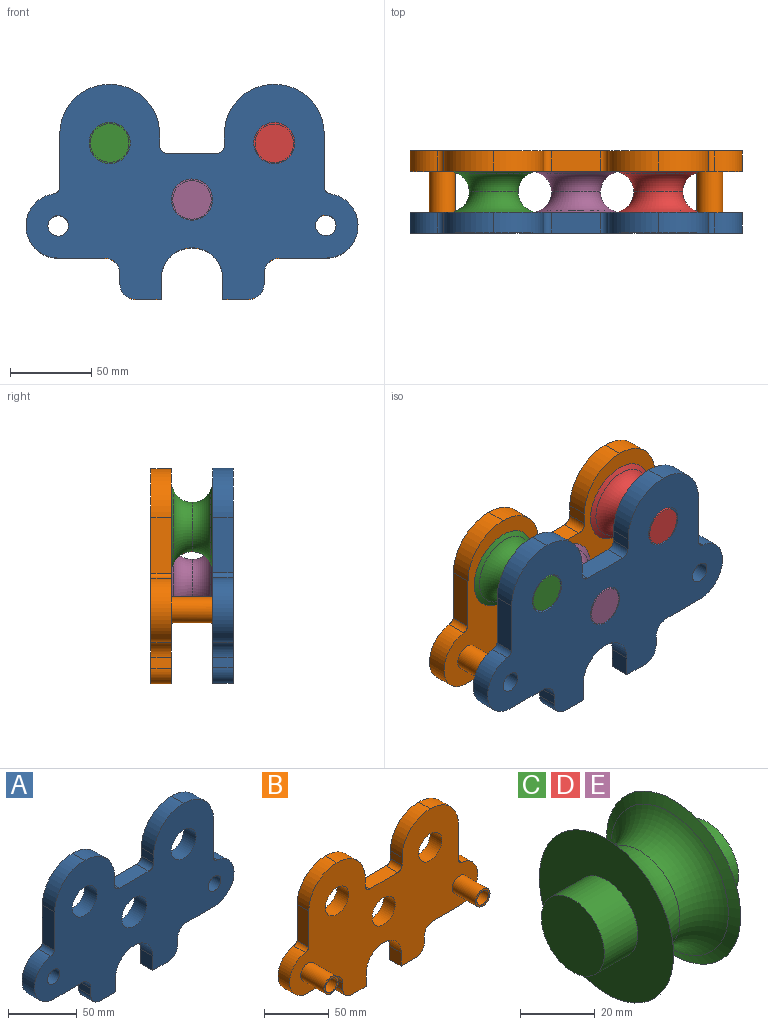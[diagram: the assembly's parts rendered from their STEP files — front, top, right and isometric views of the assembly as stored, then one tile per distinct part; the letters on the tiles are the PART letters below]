
ASSEMBLY  parts=5 mates=4
PART A: 35 faces, bbox 205x12.7x132.6 mm
  f0: plane 12.7x6.34mm, normal (1,0,0), area 80.5mm2, adj f1,f31,f33,f34
  f1: cylinder r=9.53mm len=12.7mm, axis (0,1,0), area 190mm2, adj f0,f2,f33,f34
  f2: plane 28.58x12.7mm, normal (0,0,-1), area 362.9mm2, adj f1,f3,f33,f34
  f3: cylinder r=19.93mm len=39.66mm, axis (0,1,0), area 759.2mm2, adj f2,f4,f33,f34
  f4: cylinder r=4.76mm len=12.7mm, axis (0,1,0), area 64.8mm2, adj f3,f5,f33,f34
  f5: plane 34.15x12.7mm, normal (1,0,0), area 433.7mm2, adj f4,f6,f33,f34
  f6: cylinder r=30.38mm len=30.79mm, axis (0,1,0), area 611.3mm2, adj f5,f7,f33,f34
  f7: cylinder r=30.38mm len=30.79mm, axis (0,1,0), area 611.3mm2, adj f6,f8,f33,f34
  f8: plane 12.7x7.38mm, normal (-1,0,0), area 93.7mm2, adj f7,f9,f33,f34
  f9: cylinder r=4.76mm len=12.7mm, axis (0,1,0), area 95mm2, adj f8,f10,f33,f34
  f10: plane 30.49x12.7mm, normal (0,0,1), area 387.2mm2, adj f9,f11,f33,f34
  f11: cylinder r=4.76mm len=12.7mm, axis (0,1,0), area 95mm2, adj f10,f12,f33,f34
  f12: plane 12.7x7.38mm, normal (1,0,0), area 93.7mm2, adj f11,f13,f33,f34
  f13: cylinder r=30.38mm len=30.79mm, axis (0,1,0), area 611.3mm2, adj f12,f14,f33,f34
  f14: cylinder r=30.38mm len=30.79mm, axis (0,1,0), area 611.3mm2, adj f13,f15,f33,f34
  f15: plane 34.13x12.7mm, normal (-1,0,0), area 433.5mm2, adj f14,f16,f33,f34
  f16: cylinder r=4.76mm len=12.7mm, axis (0,1,0), area 64.9mm2, adj f15,f17,f33,f34
  f17: cylinder r=19.93mm len=39.66mm, axis (0,1,0), area 759.1mm2, adj f16,f18,f33,f34
  f18: plane 28.58x12.7mm, normal (0,0,-1), area 362.9mm2, adj f17,f19,f33,f34
  f19: cylinder r=9.53mm len=12.7mm, axis (0,1,0), area 190mm2, adj f18,f20,f33,f34
  f20: plane 12.7x6.34mm, normal (-1,0,0), area 80.5mm2, adj f19,f21,f33,f34
  f21: cylinder r=9.53mm len=12.7mm, axis (0,1,0), area 190mm2, adj f20,f22,f33,f34
  f22: plane 15.88x12.7mm, normal (0,0,-1), area 201.6mm2, adj f21,f23,f33,f34
  f23: plane 12.7x12.7mm, normal (1,0,0), area 161.3mm2, adj f22,f24,f33,f34
  f24: cylinder r=19.05mm len=38.1mm, axis (0,1,0), area 760.1mm2, adj f23,f25,f33,f34
  f25: plane 12.7x12.7mm, normal (-1,0,0), area 161.3mm2, adj f24,f26,f33,f34
  f26: plane 15.88x12.7mm, normal (0,0,-1), area 201.6mm2, adj f25,f31,f33,f34
  f27: cylinder r=6.35mm len=12.7mm, axis (0,1,0), area 506.7mm2, adj f33,f34
  f28: cylinder r=12.7mm len=25.4mm, axis (0,1,0), area 1013.4mm2, adj f33,f34
  f29: cylinder r=12.7mm len=25.4mm, axis (0,1,0), area 1013.4mm2, adj f33,f34
  f30: cylinder r=12.7mm len=25.4mm, axis (0,1,0), area 1013.4mm2, adj f33,f34
  f31: cylinder r=9.53mm len=12.7mm, axis (0,1,0), area 190mm2, adj f0,f26,f33,f34
  f32: cylinder r=6.35mm len=12.7mm, axis (0,1,0), area 506.7mm2, adj f33,f34
  f33: plane 204.96x132.62mm, normal (0,-1,0), area 15774.8mm2, adj f0,f1,f2,f3,f4,f5,f6,f7
  f34: plane 204.96x132.62mm, normal (0,1,0), area 15774.8mm2, adj f0,f1,f2,f3,f4,f5,f6,f7
PART B: 39 faces, bbox 205x38.1x132.6 mm
  f0: plane 12.7x6.34mm, normal (1,0,0), area 80.5mm2, adj f1,f31,f33,f34
  f1: cylinder r=9.53mm len=12.7mm, axis (0,1,0), area 190mm2, adj f0,f2,f33,f34
  f2: plane 28.58x12.7mm, normal (0,0,-1), area 362.9mm2, adj f1,f3,f33,f34
  f3: cylinder r=19.93mm len=39.66mm, axis (0,1,0), area 759.2mm2, adj f2,f4,f33,f34
  f4: cylinder r=4.76mm len=12.7mm, axis (0,1,0), area 64.8mm2, adj f3,f5,f33,f34
  f5: plane 34.15x12.7mm, normal (1,0,0), area 433.7mm2, adj f4,f6,f33,f34
  f6: cylinder r=30.38mm len=30.79mm, axis (0,1,0), area 611.3mm2, adj f5,f7,f33,f34
  f7: cylinder r=30.38mm len=30.79mm, axis (0,1,0), area 611.3mm2, adj f6,f8,f33,f34
  f8: plane 12.7x7.38mm, normal (-1,0,0), area 93.7mm2, adj f7,f9,f33,f34
  f9: cylinder r=4.76mm len=12.7mm, axis (0,1,0), area 95mm2, adj f8,f10,f33,f34
  f10: plane 30.49x12.7mm, normal (0,0,1), area 387.2mm2, adj f9,f11,f33,f34
  f11: cylinder r=4.76mm len=12.7mm, axis (0,1,0), area 95mm2, adj f10,f12,f33,f34
  f12: plane 12.7x7.38mm, normal (1,0,0), area 93.7mm2, adj f11,f13,f33,f34
  f13: cylinder r=30.38mm len=30.79mm, axis (0,1,0), area 611.3mm2, adj f12,f14,f33,f34
  f14: cylinder r=30.38mm len=30.79mm, axis (0,1,0), area 611.3mm2, adj f13,f15,f33,f34
  f15: plane 34.13x12.7mm, normal (-1,0,0), area 433.5mm2, adj f14,f16,f33,f34
  f16: cylinder r=4.76mm len=12.7mm, axis (0,1,0), area 64.9mm2, adj f15,f17,f33,f34
  f17: cylinder r=19.93mm len=39.66mm, axis (0,1,0), area 759.1mm2, adj f16,f18,f33,f34
  f18: plane 28.58x12.7mm, normal (0,0,-1), area 362.9mm2, adj f17,f19,f33,f34
  f19: cylinder r=9.53mm len=12.7mm, axis (0,1,0), area 190mm2, adj f18,f20,f33,f34
  f20: plane 12.7x6.34mm, normal (-1,0,0), area 80.5mm2, adj f19,f21,f33,f34
  f21: cylinder r=9.53mm len=12.7mm, axis (0,1,0), area 190mm2, adj f20,f22,f33,f34
  f22: plane 15.88x12.7mm, normal (0,0,-1), area 201.6mm2, adj f21,f23,f33,f34
  f23: plane 12.7x12.7mm, normal (1,0,0), area 161.3mm2, adj f22,f24,f33,f34
  f24: cylinder r=19.05mm len=38.1mm, axis (0,1,0), area 760.1mm2, adj f23,f25,f33,f34
  f25: plane 12.7x12.7mm, normal (-1,0,0), area 161.3mm2, adj f24,f26,f33,f34
  f26: plane 15.88x12.7mm, normal (0,0,-1), area 201.6mm2, adj f25,f31,f33,f34
  f27: cylinder r=6.35mm len=38.1mm, axis (0,1,0), area 1520.1mm2, adj f34,f38
  f28: cylinder r=12.7mm len=25.4mm, axis (0,1,0), area 1013.4mm2, adj f33,f34
  f29: cylinder r=12.7mm len=25.4mm, axis (0,1,0), area 1013.4mm2, adj f33,f34
  f30: cylinder r=12.7mm len=25.4mm, axis (0,1,0), area 1013.4mm2, adj f33,f34
  f31: cylinder r=9.53mm len=12.7mm, axis (0,1,0), area 190mm2, adj f0,f26,f33,f34
  f32: cylinder r=6.35mm len=38.1mm, axis (0,1,0), area 1520.1mm2, adj f34,f36
  f33: plane 204.96x132.62mm, normal (0,-1,0), area 15632.3mm2, adj f0,f1,f2,f3,f4,f5,f6,f7
  f34: plane 204.96x132.62mm, normal (0,1,0), area 15774.8mm2, adj f0,f1,f2,f3,f4,f5,f6,f7
  f35: cylinder r=7.94mm len=25.4mm, axis (0,1,0), area 1266.8mm2, adj f33,f36
  f36: plane 15.88x15.88mm, normal (0,-1,0), area 71.3mm2, adj f32,f35
  f37: cylinder r=7.94mm len=25.4mm, axis (0,1,0), area 1266.8mm2, adj f33,f38
  f38: plane 15.88x15.88mm, normal (0,-1,0), area 71.3mm2, adj f27,f37
PART C: 10 faces, bbox 50.8x59.4x59.4 mm
  f0: plane 23.81x23.81mm, normal (1,0,0), area 445.3mm2, adj f1
  f1: cylinder r=11.91mm len=23.81mm, axis (-1,0,0), area 950.1mm2, adj f0,f2
  f2: plane 50.8x50.8mm, normal (1,0,0), area 1581.5mm2, adj f1,f3
  f3: cone r=25.4mm half-angle=65deg, axis (1,0,0), area 524.1mm2, adj f2,f4
  f4: torus R=27.44mm, axis (-1,0,0), area 1549.9mm2, adj f3,f5
  f5: torus R=27.44mm, axis (-1,0,0), area 1549.9mm2, adj f4,f6
  f6: cone r=25.4mm half-angle=65deg, axis (-1,0,0), area 524.1mm2, adj f5,f7
  f7: plane 50.8x50.8mm, normal (-1,0,0), area 1581.5mm2, adj f6,f8
  f8: cylinder r=11.91mm len=23.81mm, axis (-1,0,0), area 950.1mm2, adj f7,f9
  f9: plane 23.81x23.81mm, normal (-1,0,0), area 445.3mm2, adj f8
PART D: same geometry as C
PART E: same geometry as C
PLACE A t=(8,21.46,49.86)mm
PLACE B t=(8,59.56,49.64)mm
PLACE C rot(axis=(-0.58,-0.58,0.58),120deg) t=(-42.8,34.16,84.79)mm
PLACE D rot(axis=(0.58,-0.58,-0.58),120deg) t=(58.8,34.16,84.56)mm
PLACE E rot(axis=(0.58,0.58,0.58),120deg) t=(8,34.16,49.64)mm
MATE fastened A.f17 <-> B.f35  axis (0,1,0) through (-74.55,21.46,33.65)mm
MATE fastened E.f1 <-> B.f28  axis (0,1,0) through (8,59.56,49.64)mm
MATE fastened D.f1 <-> B.f30  axis (0,1,0) through (58.8,59.56,84.56)mm
MATE fastened C.f1 <-> A.f29  axis (0,-1,0) through (-42.8,8.76,84.79)mm
